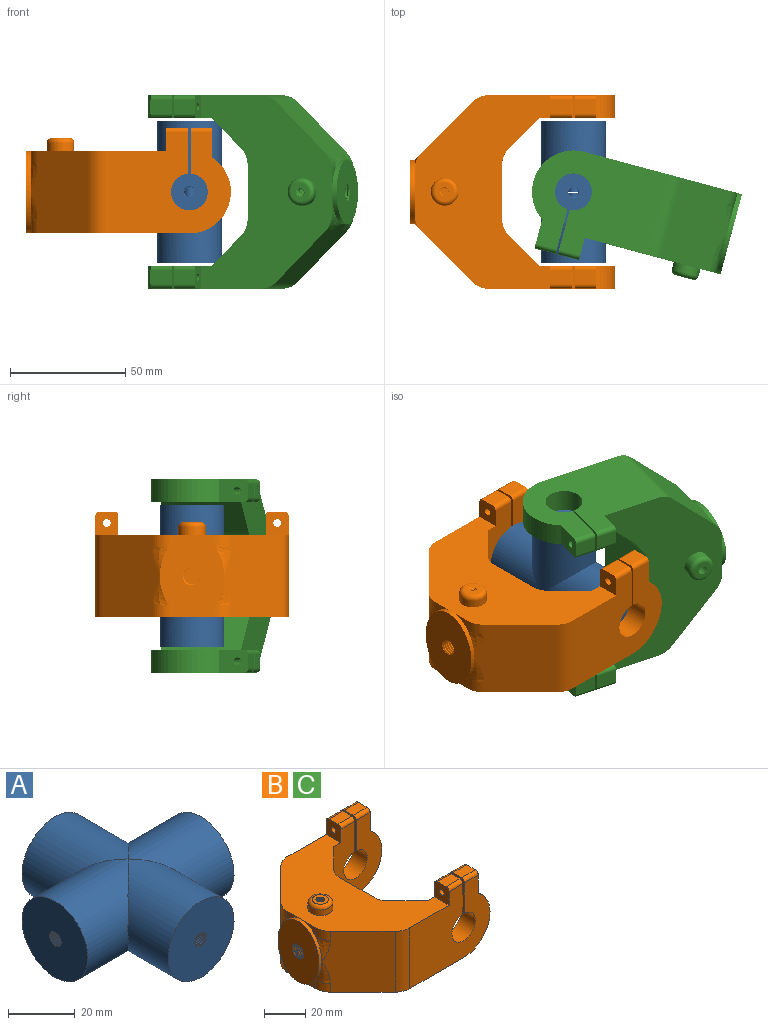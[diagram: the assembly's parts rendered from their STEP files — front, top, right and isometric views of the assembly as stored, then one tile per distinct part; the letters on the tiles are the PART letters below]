
ASSEMBLY  parts=3 mates=2
PART A: 181 faces, bbox 62.9x62.9x28.2 mm
  f0: plane 28.23x28.23mm, normal (0,-1,0), area 598.1mm2, adj f1,f39,f40,f41,f42
  f1: cylinder r=2.17mm len=4.35mm, axis (0,-1,0), area 1mm2, adj f0,f2,f39,f41
  f2: cylinder r=2.17mm len=4.35mm, axis (0,-1,0), area 2.7mm2, adj f1,f3,f39,f41
  f3: cylinder r=2.17mm len=4.35mm, axis (0,-1,0), area 2.7mm2, adj f2,f4,f39,f41
  f4: cylinder r=2.17mm len=4.35mm, axis (0,-1,0), area 2.7mm2, adj f3,f5,f39,f41
  f5: cylinder r=2.17mm len=4.35mm, axis (0,-1,0), area 2.7mm2, adj f4,f6,f39,f41
  f6: cylinder r=2.17mm len=4.35mm, axis (0,-1,0), area 2.7mm2, adj f5,f7,f39,f41
  f7: cylinder r=2.17mm len=4.35mm, axis (0,-1,0), area 2.7mm2, adj f6,f8,f39,f41
  f8: cylinder r=2.17mm len=4.35mm, axis (0,-1,0), area 2.7mm2, adj f7,f9,f39,f41
  f9: cylinder r=2.17mm len=4.35mm, axis (0,-1,0), area 2.7mm2, adj f8,f10,f39,f41
  f10: cylinder r=2.17mm len=4.35mm, axis (0,-1,0), area 2.7mm2, adj f9,f11,f39,f41
  f11: cylinder r=2.17mm len=4.35mm, axis (0,-1,0), area 2.7mm2, adj f10,f12,f39,f41
  f12: cylinder r=2.17mm len=4.35mm, axis (0,-1,0), area 2.7mm2, adj f11,f13,f39,f41
  f13: cylinder r=2.17mm len=4.35mm, axis (0,-1,0), area 2.7mm2, adj f12,f14,f39,f41
  f14: cylinder r=2.17mm len=4.35mm, axis (0,-1,0), area 2.7mm2, adj f13,f15,f39,f41
  f15: cylinder r=2.17mm len=4.35mm, axis (0,-1,0), area 2.7mm2, adj f14,f16,f39,f41
  f16: cylinder r=2.17mm len=4.35mm, axis (0,-1,0), area 2.7mm2, adj f15,f17,f39,f41
  f17: cylinder r=2.17mm len=4.35mm, axis (0,-1,0), area 2.7mm2, adj f16,f18,f39,f41
  f18: cylinder r=2.17mm len=4.35mm, axis (0,-1,0), area 2.7mm2, adj f17,f19,f39,f41
  f19: cylinder r=2.17mm len=4.35mm, axis (0,-1,0), area 2.7mm2, adj f18,f20,f39,f41
  f20: cylinder r=2.17mm len=4.35mm, axis (0,-1,0), area 2.7mm2, adj f19,f21,f39,f41
  f21: cylinder r=2.17mm len=4.35mm, axis (0,-1,0), area 2.7mm2, adj f20,f22,f39,f41
  f22: cylinder r=2.17mm len=4.35mm, axis (0,-1,0), area 2.7mm2, adj f21,f23,f39,f41
  f23: cylinder r=2.17mm len=4.35mm, axis (0,-1,0), area 2.7mm2, adj f22,f24,f39,f41
  f24: cylinder r=2.17mm len=4.35mm, axis (0,-1,0), area 2.7mm2, adj f23,f25,f39,f41
  f25: cylinder r=2.17mm len=4.35mm, axis (0,-1,0), area 2.7mm2, adj f24,f26,f39,f41
  f26: cylinder r=2.17mm len=4.35mm, axis (0,-1,0), area 2.7mm2, adj f25,f27,f39,f41
  f27: cylinder r=2.17mm len=4.35mm, axis (0,-1,0), area 2.7mm2, adj f26,f28,f39,f41
  f28: cylinder r=2.17mm len=4.35mm, axis (0,-1,0), area 2.7mm2, adj f27,f29,f39,f41
  f29: cylinder r=2.17mm len=4.35mm, axis (0,-1,0), area 2.7mm2, adj f28,f30,f39,f41
  f30: cylinder r=2.17mm len=4.35mm, axis (0,-1,0), area 2.7mm2, adj f29,f31,f39,f41
  f31: cylinder r=2.17mm len=4.35mm, axis (0,-1,0), area 2.7mm2, adj f30,f32,f39,f41
  f32: cylinder r=2.17mm len=4.35mm, axis (0,-1,0), area 4.3mm2, adj f31,f33,f38,f41
  f33: cylinder r=2.17mm len=4.53mm, axis (0,-1,0), area 49.6mm2, adj f32,f34,f35,f37,f38
  f34: cylinder r=2.62mm len=4.35mm, axis (-1,0,0), area 16.7mm2, adj f33
  f35: bspline ~5.02x4.81mm, area 3.9mm2, adj f33,f36,f37,f41
  f36: bspline ~5.11x4.93mm, area 1.8mm2, adj f35,f37,f38,f40
  f37: plane 0.14x0.06mm, normal (1,-0.01,0), area 0mm2, adj f33,f35,f36,f38
  f38: bspline ~5.02x4.81mm, area 3.9mm2, adj f32,f33,f36,f37,f39
  f39: bspline ~24.92x6.02mm, area 230.7mm2, adj f0,f1,f2,f3,f4,f5,f6,f7
  f40: bspline ~24.9x6.11mm, area 59mm2, adj f0,f36,f39,f41
  f41: bspline ~25.32x6.02mm, area 233.8mm2, adj f0,f1,f2,f3,f4,f5,f6,f7
  f42: cylinder r=14mm len=31mm, axis (0,-1,0), area 1942.9mm2, adj f0,f43,f180
  f43: cylinder r=14mm len=31mm, axis (1,0,0), area 1942.9mm2, adj f42,f44,f86
  f44: cylinder r=14mm len=31mm, axis (0,-1,0), area 1942.9mm2, adj f43,f45,f180
  f45: plane 28.23x28.23mm, normal (0,1,0), area 598.1mm2, adj f44,f46,f83,f84,f85
  f46: cylinder r=2.17mm len=4.35mm, axis (0,1,0), area 2.4mm2, adj f45,f47,f83,f85
  f47: cylinder r=2.17mm len=4.35mm, axis (0,1,0), area 2.7mm2, adj f46,f48,f83,f85
  f48: cylinder r=2.17mm len=4.35mm, axis (0,1,0), area 2.7mm2, adj f47,f49,f83,f85
  f49: cylinder r=2.17mm len=4.35mm, axis (0,1,0), area 2.7mm2, adj f48,f50,f83,f85
  f50: cylinder r=2.17mm len=4.35mm, axis (0,1,0), area 2.7mm2, adj f49,f51,f83,f85
  f51: cylinder r=2.17mm len=4.35mm, axis (0,1,0), area 2.7mm2, adj f50,f52,f83,f85
  f52: cylinder r=2.17mm len=4.35mm, axis (0,1,0), area 2.7mm2, adj f51,f53,f83,f85
  f53: cylinder r=2.17mm len=4.35mm, axis (0,1,0), area 2.7mm2, adj f52,f54,f83,f85
  f54: cylinder r=2.17mm len=4.35mm, axis (0,1,0), area 2.7mm2, adj f53,f55,f83,f85
  f55: cylinder r=2.17mm len=4.35mm, axis (0,1,0), area 2.7mm2, adj f54,f56,f83,f85
  f56: cylinder r=2.17mm len=4.35mm, axis (0,1,0), area 2.7mm2, adj f55,f57,f83,f85
  f57: cylinder r=2.17mm len=4.35mm, axis (0,1,0), area 2.7mm2, adj f56,f58,f83,f85
  f58: cylinder r=2.17mm len=4.35mm, axis (0,1,0), area 2.7mm2, adj f57,f59,f83,f85
  f59: cylinder r=2.17mm len=4.35mm, axis (0,1,0), area 2.7mm2, adj f58,f60,f83,f85
  f60: cylinder r=2.17mm len=4.35mm, axis (0,1,0), area 2.7mm2, adj f59,f61,f83,f85
  f61: cylinder r=2.17mm len=4.35mm, axis (0,1,0), area 2.7mm2, adj f60,f62,f83,f85
  f62: cylinder r=2.17mm len=4.35mm, axis (0,1,0), area 2.7mm2, adj f61,f63,f83,f85
  f63: cylinder r=2.17mm len=4.35mm, axis (0,1,0), area 2.7mm2, adj f62,f64,f83,f85
  f64: cylinder r=2.17mm len=4.35mm, axis (0,1,0), area 2.7mm2, adj f63,f65,f83,f85
  f65: cylinder r=2.17mm len=4.35mm, axis (0,1,0), area 2.7mm2, adj f64,f66,f83,f85
  f66: cylinder r=2.17mm len=4.35mm, axis (0,1,0), area 2.7mm2, adj f65,f67,f83,f85
  f67: cylinder r=2.17mm len=4.35mm, axis (0,1,0), area 2.7mm2, adj f66,f68,f83,f85
  f68: cylinder r=2.17mm len=4.35mm, axis (0,1,0), area 2.7mm2, adj f67,f69,f83,f85
  f69: cylinder r=2.17mm len=4.35mm, axis (0,1,0), area 2.7mm2, adj f68,f70,f83,f85
  f70: cylinder r=2.17mm len=4.35mm, axis (0,1,0), area 2.7mm2, adj f69,f71,f83,f85
  f71: cylinder r=2.17mm len=4.35mm, axis (0,1,0), area 2.7mm2, adj f70,f72,f83,f85
  f72: cylinder r=2.17mm len=4.35mm, axis (0,1,0), area 2.7mm2, adj f71,f73,f83,f85
  f73: cylinder r=2.17mm len=4.35mm, axis (0,1,0), area 2.7mm2, adj f72,f74,f83,f85
  f74: cylinder r=2.17mm len=4.35mm, axis (0,1,0), area 2.7mm2, adj f73,f75,f83,f85
  f75: cylinder r=2.17mm len=4.35mm, axis (0,1,0), area 2.7mm2, adj f74,f76,f83,f85
  f76: cylinder r=2.17mm len=4.35mm, axis (0,1,0), area 3.1mm2, adj f75,f77,f82,f83,f85
  f77: cylinder r=2.17mm len=4.93mm, axis (0,1,0), area 52.1mm2, adj f76,f78,f79,f81,f82,f85
  f78: cylinder r=2.62mm len=4.35mm, axis (-1,0,0), area 16.7mm2, adj f77
  f79: bspline ~5.02x4.81mm, area 3.9mm2, adj f77,f80,f81,f85
  f80: bspline ~5.11x4.93mm, area 1.8mm2, adj f79,f81,f82,f84
  f81: plane 0.14x0.06mm, normal (-1,0.01,0), area 0mm2, adj f77,f79,f80,f82
  f82: bspline ~5.02x4.81mm, area 3.9mm2, adj f76,f77,f80,f81,f83
  f83: bspline ~24.92x6.02mm, area 230.7mm2, adj f45,f46,f47,f48,f49,f50,f51,f52
  f84: bspline ~24.9x6.11mm, area 59mm2, adj f45,f80,f83,f85
  f85: bspline ~25.32x6.02mm, area 233.8mm2, adj f45,f46,f47,f48,f49,f50,f51,f52
  f86: plane 28.23x28.23mm, normal (1,0,0), area 598.1mm2, adj f43,f87,f177,f178,f179
  f87: cylinder r=2.17mm len=4.35mm, axis (-1,0,0), area 1mm2, adj f86,f88,f177,f179
  f88: cylinder r=2.17mm len=4.35mm, axis (-1,0,0), area 2.7mm2, adj f87,f89,f177,f179
  f89: cylinder r=2.17mm len=4.35mm, axis (-1,0,0), area 2.7mm2, adj f88,f90,f177,f179
  f90: cylinder r=2.17mm len=4.35mm, axis (-1,0,0), area 2.7mm2, adj f89,f91,f177,f179
  f91: cylinder r=2.17mm len=4.35mm, axis (-1,0,0), area 2.7mm2, adj f90,f92,f177,f179
  f92: cylinder r=2.17mm len=4.35mm, axis (-1,0,0), area 2.7mm2, adj f91,f93,f177,f179
  f93: cylinder r=2.17mm len=4.35mm, axis (-1,0,0), area 2.7mm2, adj f92,f94,f177,f179
  f94: cylinder r=2.17mm len=4.35mm, axis (-1,0,0), area 2.7mm2, adj f93,f95,f177,f179
  f95: cylinder r=2.17mm len=4.35mm, axis (-1,0,0), area 2.7mm2, adj f94,f96,f177,f179
  f96: cylinder r=2.17mm len=4.35mm, axis (-1,0,0), area 2.7mm2, adj f95,f97,f177,f179
  f97: cylinder r=2.17mm len=4.35mm, axis (-1,0,0), area 2.7mm2, adj f96,f98,f177,f179
  f98: cylinder r=2.17mm len=4.35mm, axis (-1,0,0), area 2.7mm2, adj f97,f99,f177,f179
  f99: cylinder r=2.17mm len=4.35mm, axis (-1,0,0), area 2.7mm2, adj f98,f100,f177,f179
  f100: cylinder r=2.17mm len=4.35mm, axis (-1,0,0), area 2.7mm2, adj f99,f101,f177,f179
  f101: cylinder r=2.17mm len=4.35mm, axis (-1,0,0), area 2.7mm2, adj f100,f102,f177,f179
  f102: cylinder r=2.17mm len=4.35mm, axis (-1,0,0), area 2.7mm2, adj f101,f103,f177,f179
  f103: cylinder r=2.17mm len=4.35mm, axis (-1,0,0), area 2.7mm2, adj f102,f104,f177,f179
  f104: cylinder r=2.17mm len=4.35mm, axis (-1,0,0), area 2.7mm2, adj f103,f105,f177,f179
  f105: cylinder r=2.17mm len=4.35mm, axis (-1,0,0), area 2.7mm2, adj f104,f106,f177,f179
  f106: cylinder r=2.17mm len=4.35mm, axis (-1,0,0), area 2.7mm2, adj f105,f107,f177,f179
  f107: cylinder r=2.17mm len=4.35mm, axis (-1,0,0), area 2.7mm2, adj f106,f108,f177,f179
  f108: cylinder r=2.17mm len=4.35mm, axis (-1,0,0), area 2.7mm2, adj f107,f109,f177,f179
  f109: cylinder r=2.17mm len=4.35mm, axis (-1,0,0), area 2.7mm2, adj f108,f110,f177,f179
  f110: cylinder r=2.17mm len=4.35mm, axis (-1,0,0), area 2.7mm2, adj f109,f111,f177,f179
  f111: cylinder r=2.17mm len=4.35mm, axis (-1,0,0), area 2.7mm2, adj f110,f112,f177,f179
  f112: cylinder r=2.17mm len=4.35mm, axis (-1,0,0), area 2.7mm2, adj f111,f113,f177,f179
  f113: cylinder r=2.17mm len=4.35mm, axis (-1,0,0), area 2.7mm2, adj f112,f114,f177,f179
  f114: cylinder r=2.17mm len=4.35mm, axis (-1,0,0), area 2.7mm2, adj f113,f115,f177,f179
  f115: cylinder r=2.17mm len=4.35mm, axis (-1,0,0), area 2.7mm2, adj f114,f116,f177,f179
  f116: cylinder r=2.17mm len=4.35mm, axis (-1,0,0), area 2.7mm2, adj f115,f117,f177,f179
  f117: cylinder r=2.17mm len=4.35mm, axis (-1,0,0), area 2.7mm2, adj f116,f118,f177,f179
  f118: cylinder r=2.17mm len=4.35mm, axis (-1,0,0), area 4.3mm2, adj f117,f119,f176,f179
  f119: cylinder r=2.17mm len=12mm, axis (-1,0,0), area 120.6mm2, adj f118,f120,f121,f122,f123,f124,f125,f126
  f120: cylinder r=2.62mm len=4.23mm, axis (0,-1,0), area 0mm2, adj f119,f122
  f121: cylinder r=2.17mm len=4.23mm, axis (0,-1,0), area 0mm2, adj f119,f122
  f122: plane 4.23x2.12mm, normal (0,1,0), area 2.4mm2, adj f119,f120,f121
  f123: cylinder r=2.17mm len=4.23mm, axis (0,-1,0), area 0mm2, adj f119,f124
  f124: plane 4.23x2.12mm, normal (0,1,0), area 2.4mm2, adj f119,f123,f125
  f125: cylinder r=2.62mm len=4.23mm, axis (0,-1,0), area 0mm2, adj f119,f124
  f126: plane 0.14x0.06mm, normal (0.01,-1,0), area 0mm2, adj f119,f127,f128,f176
  f127: bspline ~5.06x4.86mm, area 1.8mm2, adj f126,f128,f176,f178
  f128: bspline ~5.04x4.86mm, area 3.9mm2, adj f119,f126,f127,f179
  f129: cylinder r=2.62mm len=4.35mm, axis (0,1,0), area 0mm2, adj f119,f130
  f130: plane 4.35x2.63mm, normal (0,-1,0), area 2.5mm2, adj f119,f129,f131
  f131: cylinder r=2.17mm len=4.35mm, axis (0,1,0), area 0mm2, adj f130,f132
  f132: cylinder r=2.17mm len=4.35mm, axis (-1,0,0), area 0mm2, adj f131,f133
  f133: cylinder r=2.17mm len=4.35mm, axis (0,1,0), area 0mm2, adj f132,f175
  f134: cylinder r=2.62mm len=4.35mm, axis (0,1,0), area 0mm2, adj f119,f175
  f135: cylinder r=2.17mm len=4.35mm, axis (-1,0,0), area 4.3mm2, adj f119,f136,f171,f172
  f136: bspline ~25.32x6.02mm, area 233.8mm2, adj f135,f137,f139,f140,f141,f142,f143,f144
  f137: plane 28.23x28.23mm, normal (-1,0,0), area 598.1mm2, adj f136,f138,f139,f169,f180
  f138: bspline ~24.92x6.02mm, area 230.7mm2, adj f137,f139,f140,f141,f142,f143,f144,f145
  f139: cylinder r=2.17mm len=4.35mm, axis (-1,0,0), area 1mm2, adj f136,f137,f138,f140
  f140: cylinder r=2.17mm len=4.35mm, axis (-1,0,0), area 2.7mm2, adj f136,f138,f139,f141
  f141: cylinder r=2.17mm len=4.35mm, axis (-1,0,0), area 2.7mm2, adj f136,f138,f140,f142
  f142: cylinder r=2.17mm len=4.35mm, axis (-1,0,0), area 2.7mm2, adj f136,f138,f141,f143
  f143: cylinder r=2.17mm len=4.35mm, axis (-1,0,0), area 2.7mm2, adj f136,f138,f142,f144
  f144: cylinder r=2.17mm len=4.35mm, axis (-1,0,0), area 2.7mm2, adj f136,f138,f143,f145
  f145: cylinder r=2.17mm len=4.35mm, axis (-1,0,0), area 2.7mm2, adj f136,f138,f144,f146
  f146: cylinder r=2.17mm len=4.35mm, axis (-1,0,0), area 2.7mm2, adj f136,f138,f145,f147
  f147: cylinder r=2.17mm len=4.35mm, axis (-1,0,0), area 2.7mm2, adj f136,f138,f146,f148
  f148: cylinder r=2.17mm len=4.35mm, axis (-1,0,0), area 2.7mm2, adj f136,f138,f147,f149
  f149: cylinder r=2.17mm len=4.35mm, axis (-1,0,0), area 2.7mm2, adj f136,f138,f148,f150
  f150: cylinder r=2.17mm len=4.35mm, axis (-1,0,0), area 2.7mm2, adj f136,f138,f149,f151
  f151: cylinder r=2.17mm len=4.35mm, axis (-1,0,0), area 2.7mm2, adj f136,f138,f150,f152
  f152: cylinder r=2.17mm len=4.35mm, axis (-1,0,0), area 2.7mm2, adj f136,f138,f151,f153
  f153: cylinder r=2.17mm len=4.35mm, axis (-1,0,0), area 2.7mm2, adj f136,f138,f152,f154
  f154: cylinder r=2.17mm len=4.35mm, axis (-1,0,0), area 2.7mm2, adj f136,f138,f153,f155
  f155: cylinder r=2.17mm len=4.35mm, axis (-1,0,0), area 2.7mm2, adj f136,f138,f154,f156
  f156: cylinder r=2.17mm len=4.35mm, axis (-1,0,0), area 2.7mm2, adj f136,f138,f155,f157
  f157: cylinder r=2.17mm len=4.35mm, axis (-1,0,0), area 2.7mm2, adj f136,f138,f156,f158
  f158: cylinder r=2.17mm len=4.35mm, axis (-1,0,0), area 2.7mm2, adj f136,f138,f157,f159
  f159: cylinder r=2.17mm len=4.35mm, axis (-1,0,0), area 2.7mm2, adj f136,f138,f158,f160
  f160: cylinder r=2.17mm len=4.35mm, axis (-1,0,0), area 2.7mm2, adj f136,f138,f159,f161
  f161: cylinder r=2.17mm len=4.35mm, axis (-1,0,0), area 2.7mm2, adj f136,f138,f160,f162
  f162: cylinder r=2.17mm len=4.35mm, axis (-1,0,0), area 2.7mm2, adj f136,f138,f161,f163
  f163: cylinder r=2.17mm len=4.35mm, axis (-1,0,0), area 2.7mm2, adj f136,f138,f162,f164
  f164: cylinder r=2.17mm len=4.35mm, axis (-1,0,0), area 2.7mm2, adj f136,f138,f163,f165
  f165: cylinder r=2.17mm len=4.35mm, axis (-1,0,0), area 2.7mm2, adj f136,f138,f164,f166
  f166: cylinder r=2.17mm len=4.35mm, axis (-1,0,0), area 2.7mm2, adj f136,f138,f165,f167
  f167: cylinder r=2.17mm len=4.35mm, axis (-1,0,0), area 2.7mm2, adj f136,f138,f166,f168
  f168: cylinder r=2.17mm len=4.35mm, axis (-1,0,0), area 2.7mm2, adj f136,f138,f167,f171
  f169: bspline ~24.9x6.11mm, area 59mm2, adj f136,f137,f138,f170
  f170: bspline ~5.06x4.86mm, area 1.8mm2, adj f169,f172,f173,f174
  f171: cylinder r=2.17mm len=4.35mm, axis (-1,0,0), area 2.7mm2, adj f135,f136,f138,f168
  f172: bspline ~5.02x4.81mm, area 3.9mm2, adj f119,f135,f138,f170,f173
  f173: plane 0.14x0.06mm, normal (-0.01,1,0), area 0mm2, adj f119,f170,f172,f174
  f174: bspline ~5.04x4.86mm, area 3.9mm2, adj f119,f136,f170,f173
  f175: plane 4.35x2.63mm, normal (0,-1,0), area 2.5mm2, adj f119,f133,f134
  f176: bspline ~5.02x4.81mm, area 3.9mm2, adj f118,f119,f126,f127,f177
  f177: bspline ~24.92x6.02mm, area 230.7mm2, adj f86,f87,f88,f89,f90,f91,f92,f93
  f178: bspline ~24.9x6.11mm, area 59mm2, adj f86,f127,f177,f179
  f179: bspline ~25.32x6.02mm, area 233.8mm2, adj f86,f87,f88,f89,f90,f91,f92,f93
  f180: cylinder r=14mm len=31mm, axis (1,0,0), area 1942.9mm2, adj f42,f44,f137
PART B: 70 faces, bbox 89.9x84.4x46.4 mm
  f0: plane 7.85x7.84mm, normal (-1,0,0), area 44.4mm2, adj f45,f46,f47,f48
  f1: plane 4.05x3.98mm, normal (0,0,1), area 11.3mm2, adj f41,f42,f43,f44
  f2: plane 8.2x8.2mm, normal (0,0,1), area 38.9mm2, adj f41,f42,f43,f44,f61
  f3: plane 84x59mm, normal (0,0,1), area 2966.6mm2, adj f5,f7,f8,f9,f10,f16,f21,f22
  f4: plane 84x69mm, normal (0,0,-1), area 3279.7mm2, adj f5,f7,f8,f9,f10,f11,f21,f22
  f5: plane 44x33mm, normal (0,1,0), area 999.6mm2, adj f3,f4,f9,f11,f12,f13,f14,f16
  f6: plane 36.37x28.37mm, normal (-1,0,0), area 747.3mm2, adj f36,f45,f46,f47,f48
  f7: plane 36x25.07mm, normal (-0.71,-0.71,0), area 1162.6mm2, adj f3,f4,f51,f52,f57,f58,f59
  f8: plane 54.86x44mm, normal (0,-1,0), area 1786.5mm2, adj f3,f4,f11,f12,f13,f14,f16,f17
  f9: plane 36x13.07mm, normal (0.71,0.71,0), area 665.5mm2, adj f3,f4,f5,f60
  f10: plane 36x23.72mm, normal (1,0,0), area 853.8mm2, adj f3,f4,f56,f60
  f11: cylinder r=18mm len=32.97mm, axis (0,-1,0), area 459.5mm2, adj f4,f5,f8,f12
  f12: plane 13.03x10mm, normal (1,0,0), area 120.1mm2, adj f5,f8,f11,f15,f20,f68,f69
  f13: cylinder r=8mm len=16mm, axis (0,-1,0), area 492.6mm2, adj f5,f8,f14,f17
  f14: plane 20.02x10mm, normal (-1,0,0), area 189.9mm2, adj f5,f8,f13,f15,f20,f68,f69
  f15: plane 9.5x6mm, normal (0,0,1), area 57mm2, adj f12,f14,f68,f69
  f16: plane 10x10mm, normal (-1,0,0), area 89.7mm2, adj f3,f5,f8,f18,f19,f66,f67
  f17: plane 20.02x10mm, normal (1,0,0), area 189.9mm2, adj f5,f8,f13,f18,f19,f66,f67
  f18: plane 9.5x6mm, normal (0,0,1), area 57mm2, adj f16,f17,f66,f67
  f19: cylinder r=1.65mm len=9.5mm, axis (-1,0,0), area 98.5mm2, adj f16,f17
  f20: cylinder r=1.65mm len=9.5mm, axis (-1,0,0), area 98.5mm2, adj f12,f14
  f21: plane 44x33mm, normal (0,-1,0), area 999.6mm2, adj f3,f4,f24,f25,f26,f27,f28,f30
  f22: plane 36x25.07mm, normal (-0.71,0.71,0), area 1162.6mm2, adj f3,f4,f49,f50,f53,f54,f55
  f23: plane 54.86x44mm, normal (0,1,0), area 1786.5mm2, adj f3,f4,f25,f26,f27,f28,f30,f31
  f24: plane 36x13.07mm, normal (0.71,-0.71,0), area 665.5mm2, adj f3,f4,f21,f56
  f25: cylinder r=18mm len=32.97mm, axis (0,1,0), area 459.5mm2, adj f4,f21,f23,f26
  f26: plane 13.03x10mm, normal (1,0,0), area 120.1mm2, adj f21,f23,f25,f29,f34,f62,f63
  f27: cylinder r=8mm len=16mm, axis (0,1,0), area 492.6mm2, adj f21,f23,f28,f31
  f28: plane 20.02x10mm, normal (-1,0,0), area 189.9mm2, adj f21,f23,f27,f29,f34,f62,f63
  f29: plane 9.5x6mm, normal (0,0,1), area 57mm2, adj f26,f28,f62,f63
  f30: plane 10x10mm, normal (-1,0,0), area 89.7mm2, adj f3,f21,f23,f32,f33,f64,f65
  f31: plane 20.02x10mm, normal (1,0,0), area 189.9mm2, adj f21,f23,f27,f32,f33,f64,f65
  f32: plane 9.5x6mm, normal (0,0,1), area 57mm2, adj f30,f31,f64,f65
  f33: cylinder r=1.65mm len=9.5mm, axis (-1,0,0), area 98.5mm2, adj f30,f31
  f34: cylinder r=1.65mm len=9.5mm, axis (-1,0,0), area 98.5mm2, adj f26,f28
  f35: plane 9.86x5.22mm, normal (-1,0,0), area 16mm2, adj f3,f36,f54
  f36: extruded ~36x28mm, area 201.8mm2, adj f6,f35,f37,f38,f39,f50,f52,f53
  f37: plane 9.86x5.22mm, normal (-1,0,0), area 16mm2, adj f4,f36,f51
  f38: plane 9.86x5.22mm, normal (-1,0,0), area 16mm2, adj f4,f36,f49
  f39: plane 9.86x5.22mm, normal (-1,0,0), area 16mm2, adj f3,f36,f58
  f40: cylinder r=6mm len=12mm, axis (0,0,-1), area 128.2mm2, adj f3,f61
  f41: bspline ~19.7x4.86mm, area 144.6mm2, adj f1,f2,f43,f44
  f42: bspline ~19.7x4.86mm, area 143.7mm2, adj f1,f2,f43,f44
  f43: bspline ~19.45x4.93mm, area 37mm2, adj f1,f2,f41,f42
  f44: cylinder r=1.72mm len=19.14mm, axis (0,0,-1), area 7.8mm2, adj f1,f2,f41,f42
  f45: bspline ~30.81x9.53mm, area 447.2mm2, adj f0,f6,f47,f48
  f46: bspline ~31.02x9.53mm, area 446mm2, adj f0,f6,f47,f48
  f47: bspline ~30.57x9.66mm, area 113.6mm2, adj f0,f6,f45,f46
  f48: cylinder r=3.45mm len=30mm, axis (1,0,0), area 90.4mm2, adj f0,f6,f45,f46
  f49: cylinder r=10mm len=7.07mm, axis (0,0,1), area 41mm2, adj f4,f22,f38,f50
  f50: bspline ~16.14x8.73mm, area 49.2mm2, adj f22,f36,f49
  f51: cylinder r=10mm len=7.07mm, axis (0,0,1), area 41mm2, adj f4,f7,f37,f52
  f52: bspline ~16.14x8.73mm, area 49.2mm2, adj f7,f36,f51
  f53: bspline ~16.14x8.73mm, area 49.2mm2, adj f22,f36,f54
  f54: cylinder r=10mm len=7.07mm, axis (0,0,1), area 41mm2, adj f3,f22,f35,f53
  f55: cylinder r=10mm len=36mm, axis (0,0,1), area 282.7mm2, adj f3,f4,f22,f23
  f56: cylinder r=10mm len=36mm, axis (0,0,1), area 282.7mm2, adj f3,f4,f10,f24
  f57: bspline ~16.14x8.73mm, area 49.2mm2, adj f7,f36,f58
  f58: cylinder r=10mm len=7.07mm, axis (0,0,1), area 41mm2, adj f3,f7,f39,f57
  f59: cylinder r=10mm len=36mm, axis (0,0,1), area 282.7mm2, adj f3,f4,f7,f8
  f60: cylinder r=10mm len=36mm, axis (0,0,1), area 282.7mm2, adj f3,f4,f9,f10
  f61: torus R=4mm, axis (0,0,1), area 104.1mm2, adj f2,f40
  f62: cylinder r=2mm len=9.5mm, axis (1,0,0), area 29.8mm2, adj f21,f26,f28,f29
  f63: cylinder r=2mm len=9.5mm, axis (-1,0,0), area 29.8mm2, adj f23,f26,f28,f29
  f64: cylinder r=2mm len=9.5mm, axis (-1,0,0), area 29.8mm2, adj f23,f30,f31,f32
  f65: cylinder r=2mm len=9.5mm, axis (1,0,0), area 29.8mm2, adj f21,f30,f31,f32
  f66: cylinder r=2mm len=9.5mm, axis (-1,0,0), area 29.8mm2, adj f8,f16,f17,f18
  f67: cylinder r=2mm len=9.5mm, axis (1,0,0), area 29.8mm2, adj f5,f16,f17,f18
  f68: cylinder r=2mm len=9.5mm, axis (-1,0,0), area 29.8mm2, adj f8,f12,f14,f15
  f69: cylinder r=2mm len=9.5mm, axis (1,0,0), area 29.8mm2, adj f5,f12,f14,f15
PART C: same geometry as B
PLACE A rot(axis=(0,1,0),90deg) t=(42.8,0,50.5)mm
PLACE B rot(axis=(0,1,0),0deg) t=(19.8,0,-8.5)mm
PLACE C rot(axis=(-0.09,-0.7,0.7),169.4deg) t=(105.06,6.78,9.5)mm
MATE revolute C.f11 <-> A.f34  axis (0,0,-1) through (60.8,0,41.5)mm
MATE revolute B.f11 <-> A.f1  axis (0,1,0) through (60.8,32,9.5)mm
